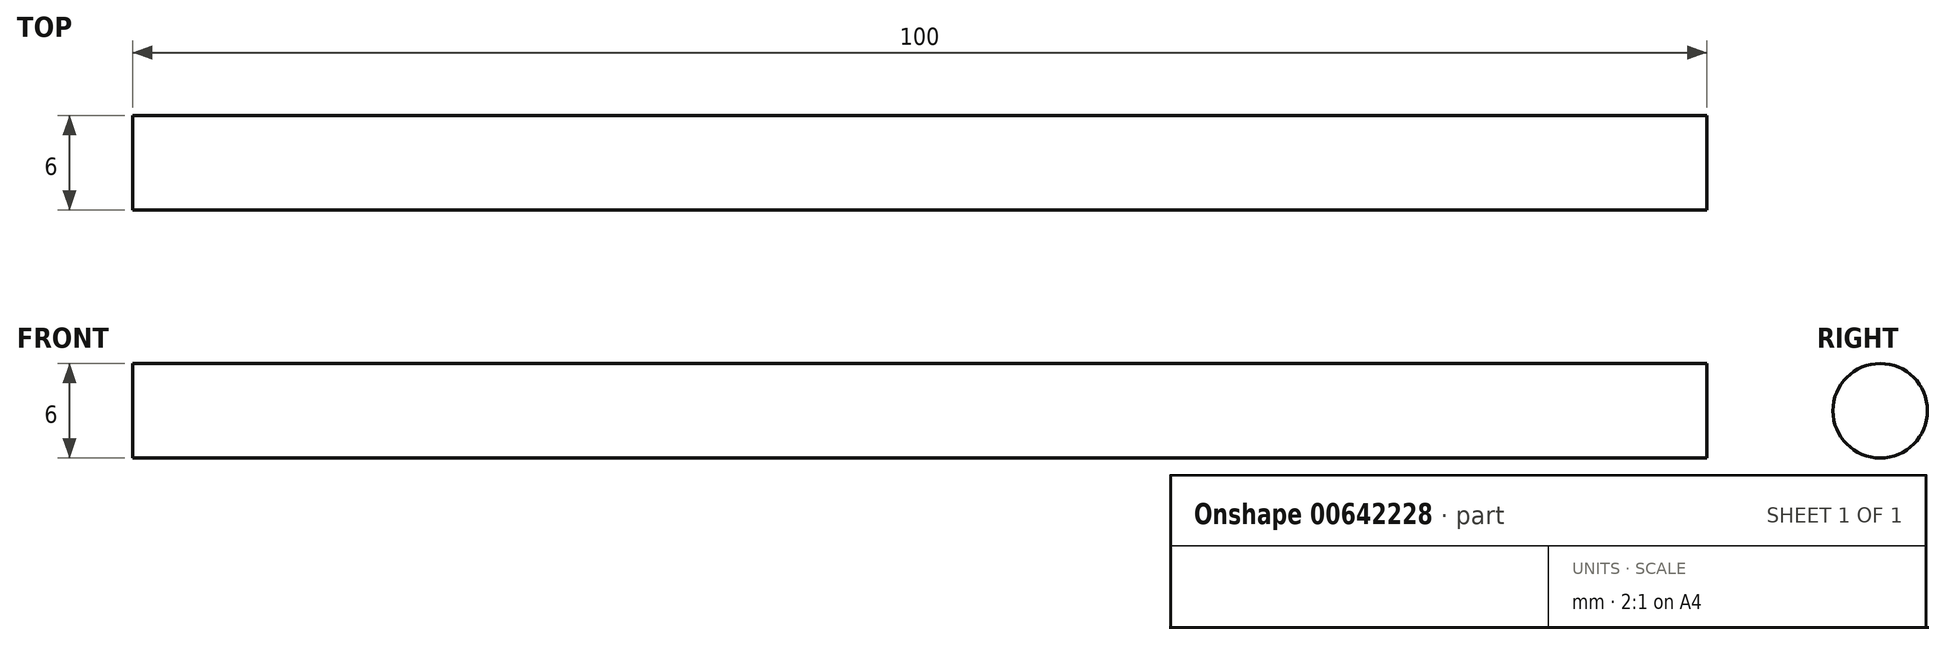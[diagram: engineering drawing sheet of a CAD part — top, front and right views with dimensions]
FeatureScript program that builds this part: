
annotation { "Feature Type Name" : "Feature", "Feature Type Description" : "" }
export const myFeature = defineFeature(function(context is Context, id is Id, definition is map)
    precondition{}
    {
        {
            var Q0;
            Q0=qCreatedBy(makeId("Right.planeOp"),FACE);
            var sketch = newSketch(context, id + "F0", { "sketchPlane" : qUnion([Q0])});
            skCircle(sketch, "E0", {"center": v(0, 0) * mm, "radius": 3 * mm});
            skSolve(sketch);
        }
        {
            var Q0;
            Q0=makeQuery(id+"F0.imprint","IMPRINT",FACE,{"disambiguationData":[TD([[makeQuery(id+"F0.imprint","IMPRINT",EDGE,{"derivedFrom":sQuery(id+"F0.wireOp",EDGE,"E0")}),1.0]])]});
            extrude(context, id + "F1", {"entities" : qUnion([Q0]), "depth" : 100 * mm, "offsetDistance" : 25 * mm});
        }
    });
